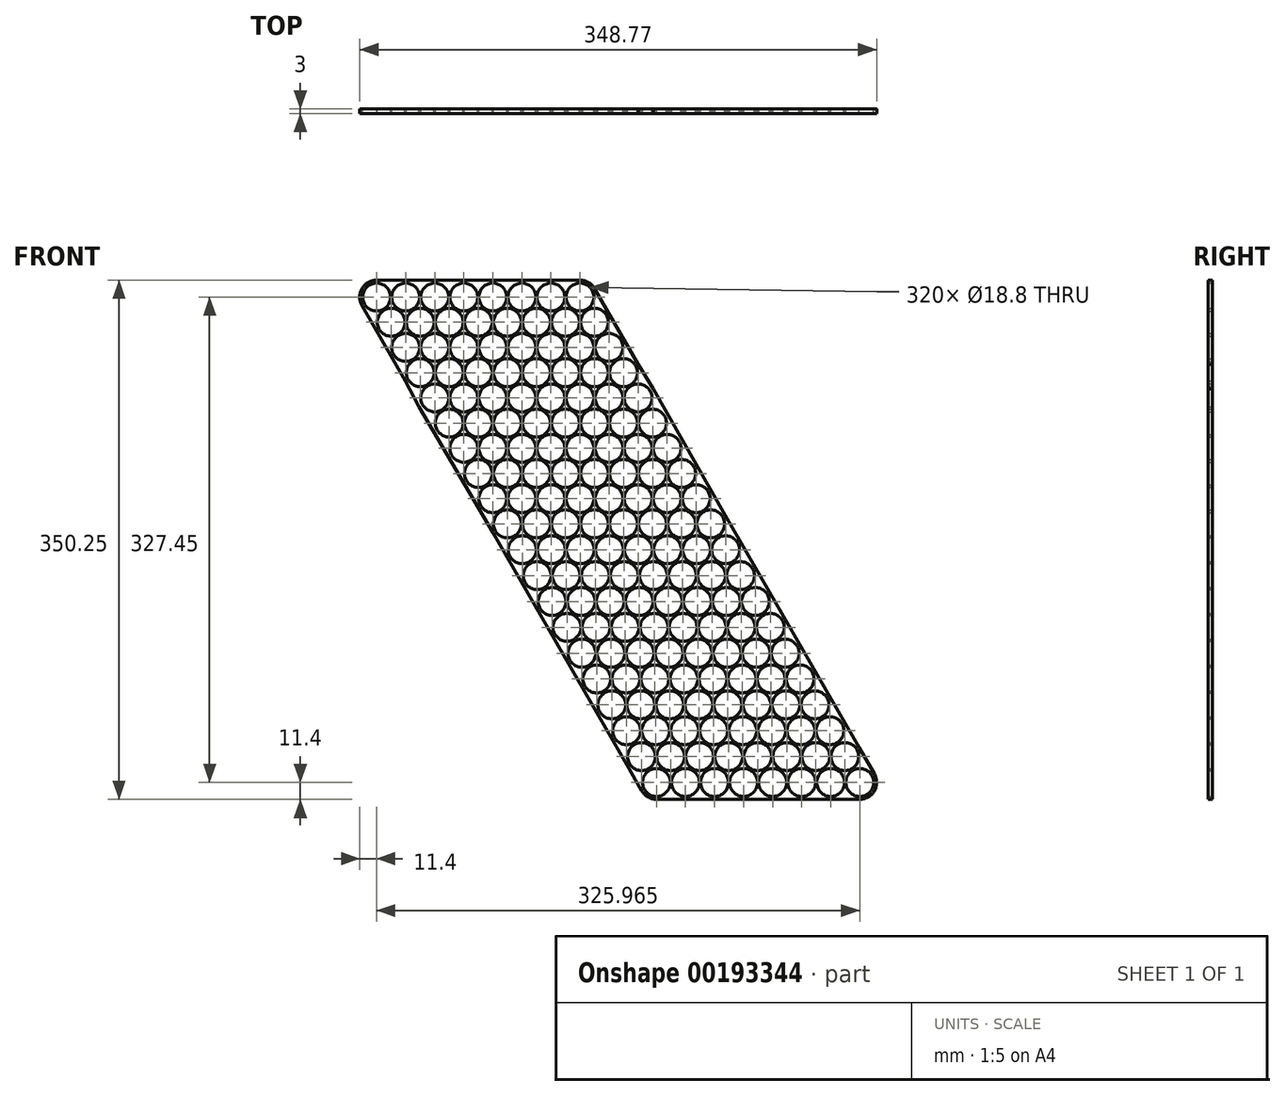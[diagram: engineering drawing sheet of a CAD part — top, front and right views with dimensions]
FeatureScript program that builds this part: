
annotation { "Feature Type Name" : "Feature", "Feature Type Description" : "" }
export const myFeature = defineFeature(function(context is Context, id is Id, definition is map)
    precondition{}
    {
        {
            var Q0;
            Q0=qCreatedBy(makeId("Front.planeOp"),FACE);
            var sketch = newSketch(context, id + "F0", { "sketchPlane" : qUnion([Q0])});
            skCircle(sketch, "E0", {"center": v(0, 0) * mm, "radius": 9.4 * mm});
            skCircle(sketch, "E1.1.0.0", {"center": v(19.6, 0) * mm, "radius": 9.4 * mm});
            skCircle(sketch, "E1.2.0.0", {"center": v(39.2, 0) * mm, "radius": 9.4 * mm});
            skCircle(sketch, "E1.3.0.0", {"center": v(58.8, 0) * mm, "radius": 9.4 * mm});
            skLineSegment(sketch, "E1.direction1", {"start": v(0, 0) * mm, "end": v(19.6, 0) * mm, "construction": true});
            skLineSegment(sketch, "E2", {"start": v(0, -17) * mm, "end": v(73.2, -17) * mm, "construction": true});
            skLineSegment(sketch, "E3", {"start": v(9.8, 0) * mm, "end": v(9.8, -17) * mm, "construction": true});
            skCircle(sketch, "E4", {"center": v(9.8, -17) * mm, "radius": 9.4 * mm});
            skCircle(sketch, "E5.1.0.0", {"center": v(29.4, -17) * mm, "radius": 9.4 * mm});
            skCircle(sketch, "E5.2.0.0", {"center": v(49, -17) * mm, "radius": 9.4 * mm});
            skCircle(sketch, "E5.3.0.0", {"center": v(68.6, -17) * mm, "radius": 9.4 * mm});
            skLineSegment(sketch, "E5.direction1", {"start": v(9.8, -17) * mm, "end": v(29.4, -17) * mm, "construction": true});
            skLineSegment(sketch, "E6", {"start": v(-8.14, -4.7) * mm, "end": v(1.66, -21.7) * mm});
            skLineSegment(sketch, "E7", {"start": v(0, 9.4) * mm, "end": v(58.8, 9.4) * mm});
            skLineSegment(sketch, "E8", {"start": v(9.8, -17) * mm, "end": v(9.8, -26.4) * mm, "construction": true});
            skLineSegment(sketch, "E9", {"start": v(68.6, -17) * mm, "end": v(68.6, -26.4) * mm, "construction": true});
            skArc(sketch, "E10", {"start": v(58.8, 9.4) * mm, "mid": v(63.5, 8.14) * mm, "end": v(66.94, 4.7) * mm});
            skArc(sketch, "E11", {"start": v(76.74, -12.3) * mm, "mid": v(76.74, -21.7) * mm, "end": v(68.6, -26.4) * mm});
            skArc(sketch, "E12", {"start": v(9.8, -26.4) * mm, "mid": v(5.1, -25.14) * mm, "end": v(1.66, -21.7) * mm});
            skArc(sketch, "E13", {"start": v(-8.14, -4.7) * mm, "mid": v(-8.14, 4.7) * mm, "end": v(0, 9.4) * mm});
            skArc(sketch, "E14.0", {"start": v(0, 11.4) * mm, "mid": v(-9.87, 5.7) * mm, "end": v(-9.88, -5.7) * mm});
            skLineSegment(sketch, "E15.0", {"start": v(0, 11.4) * mm, "end": v(58.8, 11.4) * mm});
            skLineSegment(sketch, "E16.0", {"start": v(-9.88, -5.7) * mm, "end": v(-0.08, -22.7) * mm});
            skArc(sketch, "E17.trimOffspring", {"start": v(9.8, -5.82) * mm, "mid": v(9.87, -5.71) * mm, "end": v(9.93, -5.6) * mm});
            skArc(sketch, "E18.trimOffspring", {"start": v(9.93, -5.6) * mm, "mid": v(9.86, -5.6) * mm, "end": v(9.8, -5.6) * mm});
            skCircle(sketch, "E19.0.4.0", {"center": v(78.4, 0) * mm, "radius": 9.4 * mm});
            skCircle(sketch, "E19.0.5.0", {"center": v(98, 0) * mm, "radius": 9.4 * mm});
            skCircle(sketch, "E20.0.4.0", {"center": v(88.2, -17) * mm, "radius": 9.4 * mm});
            skCircle(sketch, "E20.0.5.0", {"center": v(107.8, -17) * mm, "radius": 9.4 * mm});
            skLineSegment(sketch, "E21", {"start": v(58.8, 11.4) * mm, "end": v(98, 11.4) * mm});
            skLineSegment(sketch, "E22", {"start": v(0, 0) * mm, "end": v(9.8, -17) * mm, "construction": true});
            skCircle(sketch, "E23.1.0.0", {"center": v(19.6, -34) * mm, "radius": 9.4 * mm});
            skCircle(sketch, "E23.2.0.0", {"center": v(29.4, -51) * mm, "radius": 9.4 * mm});
            skLineSegment(sketch, "E23.direction1", {"start": v(9.8, -17) * mm, "end": v(19.6, -34) * mm, "construction": true});
            skCircle(sketch, "E24.1.0.0", {"center": v(39.2, -34) * mm, "radius": 9.4 * mm});
            skCircle(sketch, "E24.1.0.1", {"center": v(49, -51) * mm, "radius": 9.4 * mm});
            skCircle(sketch, "E24.2.0.0", {"center": v(58.8, -34) * mm, "radius": 9.4 * mm});
            skCircle(sketch, "E24.2.0.1", {"center": v(68.6, -51) * mm, "radius": 9.4 * mm});
            skCircle(sketch, "E24.3.0.0", {"center": v(78.4, -34) * mm, "radius": 9.4 * mm});
            skCircle(sketch, "E24.3.0.1", {"center": v(88.2, -51) * mm, "radius": 9.4 * mm});
            skCircle(sketch, "E24.4.0.0", {"center": v(98, -34) * mm, "radius": 9.4 * mm});
            skCircle(sketch, "E24.4.0.1", {"center": v(107.8, -51) * mm, "radius": 9.4 * mm});
            skCircle(sketch, "E24.5.0.0", {"center": v(117.6, -34) * mm, "radius": 9.4 * mm});
            skCircle(sketch, "E24.5.0.1", {"center": v(127.4, -51) * mm, "radius": 9.4 * mm});
            skLineSegment(sketch, "E24.direction1", {"start": v(19.6, -34) * mm, "end": v(39.2, -34) * mm, "construction": true});
            skLineSegment(sketch, "E25", {"start": v(-0.08, -22.7) * mm, "end": v(19.52, -56.7) * mm});
            skArc(sketch, "E26.0", {"start": v(29.27, -62.4) * mm, "mid": v(29.33, -62.4) * mm, "end": v(29.4, -62.4) * mm});
            skCircle(sketch, "E27.0.6.0", {"center": v(117.6, 0) * mm, "radius": 9.4 * mm});
            skCircle(sketch, "E27.0.7.0", {"center": v(137.2, 0) * mm, "radius": 9.4 * mm});
            skCircle(sketch, "E28.0.6.0", {"center": v(127.4, -17) * mm, "radius": 9.4 * mm});
            skCircle(sketch, "E28.0.7.0", {"center": v(147, -17) * mm, "radius": 9.4 * mm});
            skCircle(sketch, "E29.0.6.0", {"center": v(137.2, -34) * mm, "radius": 9.4 * mm});
            skCircle(sketch, "E29.2.6.0", {"center": v(147, -51) * mm, "radius": 9.4 * mm});
            skCircle(sketch, "E29.0.7.0", {"center": v(156.8, -34) * mm, "radius": 9.4 * mm});
            skCircle(sketch, "E29.2.7.0", {"center": v(166.6, -51) * mm, "radius": 9.4 * mm});
            skArc(sketch, "E30.0", {"start": v(147.08, 5.7) * mm, "mid": v(142.9, 9.87) * mm, "end": v(137.2, 11.4) * mm});
            skLineSegment(sketch, "E31", {"start": v(98, 11.4) * mm, "end": v(137.2, 11.4) * mm});
            skLineSegment(sketch, "E32", {"start": v(147.08, 5.7) * mm, "end": v(176.48, -45.3) * mm});
            skCircle(sketch, "E33.0.3.0", {"center": v(39.2, -68) * mm, "radius": 9.4 * mm});
            skCircle(sketch, "E34.1.0.0", {"center": v(58.8, -68) * mm, "radius": 9.4 * mm});
            skCircle(sketch, "E34.2.0.0", {"center": v(78.4, -68) * mm, "radius": 9.4 * mm});
            skCircle(sketch, "E34.3.0.0", {"center": v(98, -68) * mm, "radius": 9.4 * mm});
            skCircle(sketch, "E34.4.0.0", {"center": v(117.6, -68) * mm, "radius": 9.4 * mm});
            skCircle(sketch, "E34.5.0.0", {"center": v(137.2, -68) * mm, "radius": 9.4 * mm});
            skCircle(sketch, "E34.6.0.0", {"center": v(156.8, -68) * mm, "radius": 9.4 * mm});
            skCircle(sketch, "E34.7.0.0", {"center": v(176.4, -68) * mm, "radius": 9.4 * mm});
            skLineSegment(sketch, "E34.direction1", {"start": v(39.2, -68) * mm, "end": v(58.8, -68) * mm, "construction": true});
            skLineSegment(sketch, "E35", {"start": v(19.52, -56.7) * mm, "end": v(28.57, -74.14) * mm});
            skLineSegment(sketch, "E36", {"start": v(176.48, -45.3) * mm, "end": v(186.68, -62.07) * mm});
            skCircle(sketch, "E37.1.0.0", {"center": v(49, -85) * mm, "radius": 9.4 * mm});
            skCircle(sketch, "E37.1.0.1", {"center": v(68.6, -85) * mm, "radius": 9.4 * mm});
            skCircle(sketch, "E37.1.0.2", {"center": v(88.2, -85) * mm, "radius": 9.4 * mm});
            skCircle(sketch, "E37.1.0.3", {"center": v(107.8, -85) * mm, "radius": 9.4 * mm});
            skCircle(sketch, "E37.1.0.4", {"center": v(127.4, -85) * mm, "radius": 9.4 * mm});
            skCircle(sketch, "E37.1.0.5", {"center": v(147, -85) * mm, "radius": 9.4 * mm});
            skCircle(sketch, "E37.1.0.6", {"center": v(166.6, -85) * mm, "radius": 9.4 * mm});
            skCircle(sketch, "E37.1.0.7", {"center": v(186.2, -85) * mm, "radius": 9.4 * mm});
            skCircle(sketch, "E37.2.0.0", {"center": v(58.8, -102) * mm, "radius": 9.4 * mm});
            skCircle(sketch, "E37.2.0.1", {"center": v(78.4, -102) * mm, "radius": 9.4 * mm});
            skCircle(sketch, "E37.2.0.2", {"center": v(98, -102) * mm, "radius": 9.4 * mm});
            skCircle(sketch, "E37.2.0.3", {"center": v(117.6, -102) * mm, "radius": 9.4 * mm});
            skCircle(sketch, "E37.2.0.4", {"center": v(137.2, -102) * mm, "radius": 9.4 * mm});
            skCircle(sketch, "E37.2.0.5", {"center": v(156.8, -102) * mm, "radius": 9.4 * mm});
            skCircle(sketch, "E37.2.0.6", {"center": v(176.4, -102) * mm, "radius": 9.4 * mm});
            skCircle(sketch, "E37.2.0.7", {"center": v(196, -102) * mm, "radius": 9.4 * mm});
            skCircle(sketch, "E37.3.0.0", {"center": v(68.6, -119) * mm, "radius": 9.4 * mm});
            skCircle(sketch, "E37.3.0.1", {"center": v(88.2, -119) * mm, "radius": 9.4 * mm});
            skCircle(sketch, "E37.3.0.2", {"center": v(107.8, -119) * mm, "radius": 9.4 * mm});
            skCircle(sketch, "E37.3.0.3", {"center": v(127.4, -119) * mm, "radius": 9.4 * mm});
            skCircle(sketch, "E37.3.0.4", {"center": v(147, -119) * mm, "radius": 9.4 * mm});
            skCircle(sketch, "E37.3.0.5", {"center": v(166.6, -119) * mm, "radius": 9.4 * mm});
            skCircle(sketch, "E37.3.0.6", {"center": v(186.2, -119) * mm, "radius": 9.4 * mm});
            skCircle(sketch, "E37.3.0.7", {"center": v(205.8, -119) * mm, "radius": 9.4 * mm});
            skCircle(sketch, "E37.4.0.0", {"center": v(78.4, -136) * mm, "radius": 9.4 * mm});
            skCircle(sketch, "E37.4.0.1", {"center": v(98, -136) * mm, "radius": 9.4 * mm});
            skCircle(sketch, "E37.4.0.2", {"center": v(117.6, -136) * mm, "radius": 9.4 * mm});
            skCircle(sketch, "E37.4.0.3", {"center": v(137.2, -136) * mm, "radius": 9.4 * mm});
            skCircle(sketch, "E37.4.0.4", {"center": v(156.8, -136) * mm, "radius": 9.4 * mm});
            skCircle(sketch, "E37.4.0.5", {"center": v(176.4, -136) * mm, "radius": 9.4 * mm});
            skCircle(sketch, "E37.4.0.6", {"center": v(196, -136) * mm, "radius": 9.4 * mm});
            skCircle(sketch, "E37.4.0.7", {"center": v(215.6, -136) * mm, "radius": 9.4 * mm});
            skCircle(sketch, "E37.5.0.0", {"center": v(88.2, -153) * mm, "radius": 9.4 * mm});
            skCircle(sketch, "E37.5.0.1", {"center": v(107.8, -153) * mm, "radius": 9.4 * mm});
            skCircle(sketch, "E37.5.0.2", {"center": v(127.4, -153) * mm, "radius": 9.4 * mm});
            skCircle(sketch, "E37.5.0.3", {"center": v(147, -153) * mm, "radius": 9.4 * mm});
            skCircle(sketch, "E37.5.0.4", {"center": v(166.6, -153) * mm, "radius": 9.4 * mm});
            skCircle(sketch, "E37.5.0.5", {"center": v(186.2, -153) * mm, "radius": 9.4 * mm});
            skCircle(sketch, "E37.5.0.6", {"center": v(205.8, -153) * mm, "radius": 9.4 * mm});
            skCircle(sketch, "E37.5.0.7", {"center": v(225.4, -153) * mm, "radius": 9.4 * mm});
            skLineSegment(sketch, "E37.direction1", {"start": v(39.2, -68) * mm, "end": v(49, -85) * mm, "construction": true});
            skLineSegment(sketch, "E38", {"start": v(28.57, -74.14) * mm, "end": v(78.37, -158.78) * mm});
            skLineSegment(sketch, "E39", {"start": v(186.68, -62.07) * mm, "end": v(235.3, -147.35) * mm});
            skCircle(sketch, "E40.1.0.0", {"center": v(98.25, -170.44) * mm, "radius": 9.4 * mm});
            skCircle(sketch, "E40.1.0.1", {"center": v(117.85, -170.44) * mm, "radius": 9.4 * mm});
            skCircle(sketch, "E40.1.0.2", {"center": v(137.45, -170.44) * mm, "radius": 9.4 * mm});
            skCircle(sketch, "E40.1.0.3", {"center": v(157.05, -170.44) * mm, "radius": 9.4 * mm});
            skCircle(sketch, "E40.1.0.4", {"center": v(176.65, -170.44) * mm, "radius": 9.4 * mm});
            skCircle(sketch, "E40.1.0.5", {"center": v(196.25, -170.44) * mm, "radius": 9.4 * mm});
            skCircle(sketch, "E40.1.0.6", {"center": v(215.85, -170.44) * mm, "radius": 9.4 * mm});
            skCircle(sketch, "E40.1.0.7", {"center": v(235.45, -170.44) * mm, "radius": 9.4 * mm});
            skCircle(sketch, "E40.2.0.0", {"center": v(108.31, -187.89) * mm, "radius": 9.4 * mm});
            skCircle(sketch, "E40.2.0.1", {"center": v(127.91, -187.89) * mm, "radius": 9.4 * mm});
            skCircle(sketch, "E40.2.0.2", {"center": v(147.51, -187.89) * mm, "radius": 9.4 * mm});
            skCircle(sketch, "E40.2.0.3", {"center": v(167.11, -187.89) * mm, "radius": 9.4 * mm});
            skCircle(sketch, "E40.2.0.4", {"center": v(186.71, -187.89) * mm, "radius": 9.4 * mm});
            skCircle(sketch, "E40.2.0.5", {"center": v(206.31, -187.89) * mm, "radius": 9.4 * mm});
            skCircle(sketch, "E40.2.0.6", {"center": v(225.91, -187.89) * mm, "radius": 9.4 * mm});
            skCircle(sketch, "E40.2.0.7", {"center": v(245.51, -187.89) * mm, "radius": 9.4 * mm});
            skCircle(sketch, "E40.3.0.0", {"center": v(118.37, -205.33) * mm, "radius": 9.4 * mm});
            skCircle(sketch, "E40.3.0.1", {"center": v(137.97, -205.33) * mm, "radius": 9.4 * mm});
            skCircle(sketch, "E40.3.0.2", {"center": v(157.57, -205.33) * mm, "radius": 9.4 * mm});
            skCircle(sketch, "E40.3.0.3", {"center": v(177.17, -205.33) * mm, "radius": 9.4 * mm});
            skCircle(sketch, "E40.3.0.4", {"center": v(196.77, -205.33) * mm, "radius": 9.4 * mm});
            skCircle(sketch, "E40.3.0.5", {"center": v(216.37, -205.33) * mm, "radius": 9.4 * mm});
            skCircle(sketch, "E40.3.0.6", {"center": v(235.97, -205.33) * mm, "radius": 9.4 * mm});
            skCircle(sketch, "E40.3.0.7", {"center": v(255.57, -205.33) * mm, "radius": 9.4 * mm});
            skCircle(sketch, "E40.4.0.0", {"center": v(128.43, -222.78) * mm, "radius": 9.4 * mm});
            skCircle(sketch, "E40.4.0.1", {"center": v(148.03, -222.78) * mm, "radius": 9.4 * mm});
            skCircle(sketch, "E40.4.0.2", {"center": v(167.63, -222.78) * mm, "radius": 9.4 * mm});
            skCircle(sketch, "E40.4.0.3", {"center": v(187.23, -222.78) * mm, "radius": 9.4 * mm});
            skCircle(sketch, "E40.4.0.4", {"center": v(206.83, -222.78) * mm, "radius": 9.4 * mm});
            skCircle(sketch, "E40.4.0.5", {"center": v(226.43, -222.78) * mm, "radius": 9.4 * mm});
            skCircle(sketch, "E40.4.0.6", {"center": v(246.03, -222.78) * mm, "radius": 9.4 * mm});
            skCircle(sketch, "E40.4.0.7", {"center": v(265.63, -222.78) * mm, "radius": 9.4 * mm});
            skCircle(sketch, "E40.5.0.0", {"center": v(138.48, -240.22) * mm, "radius": 9.4 * mm});
            skCircle(sketch, "E40.5.0.1", {"center": v(158.08, -240.22) * mm, "radius": 9.4 * mm});
            skCircle(sketch, "E40.5.0.2", {"center": v(177.68, -240.22) * mm, "radius": 9.4 * mm});
            skCircle(sketch, "E40.5.0.3", {"center": v(197.28, -240.22) * mm, "radius": 9.4 * mm});
            skCircle(sketch, "E40.5.0.4", {"center": v(216.88, -240.22) * mm, "radius": 9.4 * mm});
            skCircle(sketch, "E40.5.0.5", {"center": v(236.48, -240.22) * mm, "radius": 9.4 * mm});
            skCircle(sketch, "E40.5.0.6", {"center": v(256.08, -240.22) * mm, "radius": 9.4 * mm});
            skCircle(sketch, "E40.5.0.7", {"center": v(275.68, -240.22) * mm, "radius": 9.4 * mm});
            skCircle(sketch, "E40.6.0.0", {"center": v(148.54, -257.67) * mm, "radius": 9.4 * mm});
            skCircle(sketch, "E40.6.0.1", {"center": v(168.14, -257.67) * mm, "radius": 9.4 * mm});
            skCircle(sketch, "E40.6.0.2", {"center": v(187.74, -257.67) * mm, "radius": 9.4 * mm});
            skCircle(sketch, "E40.6.0.3", {"center": v(207.34, -257.67) * mm, "radius": 9.4 * mm});
            skCircle(sketch, "E40.6.0.4", {"center": v(226.94, -257.67) * mm, "radius": 9.4 * mm});
            skCircle(sketch, "E40.6.0.5", {"center": v(246.54, -257.67) * mm, "radius": 9.4 * mm});
            skCircle(sketch, "E40.6.0.6", {"center": v(266.14, -257.67) * mm, "radius": 9.4 * mm});
            skCircle(sketch, "E40.6.0.7", {"center": v(285.74, -257.67) * mm, "radius": 9.4 * mm});
            skCircle(sketch, "E40.7.0.0", {"center": v(158.6, -275.11) * mm, "radius": 9.4 * mm});
            skCircle(sketch, "E40.7.0.1", {"center": v(178.2, -275.11) * mm, "radius": 9.4 * mm});
            skCircle(sketch, "E40.7.0.2", {"center": v(197.8, -275.11) * mm, "radius": 9.4 * mm});
            skCircle(sketch, "E40.7.0.3", {"center": v(217.4, -275.11) * mm, "radius": 9.4 * mm});
            skCircle(sketch, "E40.7.0.4", {"center": v(237, -275.11) * mm, "radius": 9.4 * mm});
            skCircle(sketch, "E40.7.0.5", {"center": v(256.6, -275.11) * mm, "radius": 9.4 * mm});
            skCircle(sketch, "E40.7.0.6", {"center": v(276.2, -275.11) * mm, "radius": 9.4 * mm});
            skCircle(sketch, "E40.7.0.7", {"center": v(295.8, -275.11) * mm, "radius": 9.4 * mm});
            skCircle(sketch, "E40.8.0.0", {"center": v(168.65, -292.56) * mm, "radius": 9.4 * mm});
            skCircle(sketch, "E40.8.0.1", {"center": v(188.25, -292.56) * mm, "radius": 9.4 * mm});
            skCircle(sketch, "E40.8.0.2", {"center": v(207.85, -292.56) * mm, "radius": 9.4 * mm});
            skCircle(sketch, "E40.8.0.3", {"center": v(227.45, -292.56) * mm, "radius": 9.4 * mm});
            skCircle(sketch, "E40.8.0.4", {"center": v(247.05, -292.56) * mm, "radius": 9.4 * mm});
            skCircle(sketch, "E40.8.0.5", {"center": v(266.65, -292.56) * mm, "radius": 9.4 * mm});
            skCircle(sketch, "E40.8.0.6", {"center": v(286.25, -292.56) * mm, "radius": 9.4 * mm});
            skCircle(sketch, "E40.8.0.7", {"center": v(305.85, -292.56) * mm, "radius": 9.4 * mm});
            skCircle(sketch, "E40.9.0.0", {"center": v(178.7, -310) * mm, "radius": 9.4 * mm});
            skCircle(sketch, "E40.9.0.1", {"center": v(198.3, -310) * mm, "radius": 9.4 * mm});
            skCircle(sketch, "E40.9.0.2", {"center": v(217.9, -310) * mm, "radius": 9.4 * mm});
            skCircle(sketch, "E40.9.0.3", {"center": v(237.5, -310) * mm, "radius": 9.4 * mm});
            skCircle(sketch, "E40.9.0.4", {"center": v(257.1, -310) * mm, "radius": 9.4 * mm});
            skCircle(sketch, "E40.9.0.5", {"center": v(276.7, -310) * mm, "radius": 9.4 * mm});
            skCircle(sketch, "E40.9.0.6", {"center": v(296.3, -310) * mm, "radius": 9.4 * mm});
            skCircle(sketch, "E40.9.0.7", {"center": v(315.9, -310) * mm, "radius": 9.4 * mm});
            skLineSegment(sketch, "E40.direction1", {"start": v(88.2, -153) * mm, "end": v(98.25, -170.44) * mm, "construction": true});
            skLineSegment(sketch, "E41.0", {"start": v(168.83, -315.7) * mm, "end": v(168.83, -315.7) * mm});
            skLineSegment(sketch, "E42", {"start": v(235.3, -147.35) * mm, "end": v(325.79, -304.31) * mm});
            skLineSegment(sketch, "E43", {"start": v(78.37, -158.78) * mm, "end": v(168.83, -315.7) * mm});
            skCircle(sketch, "E44.0.10.0", {"center": v(188.77, -327.45) * mm, "radius": 9.4 * mm});
            skCircle(sketch, "E44.2.10.0", {"center": v(208.37, -327.45) * mm, "radius": 9.4 * mm});
            skCircle(sketch, "E44.4.10.0", {"center": v(227.97, -327.45) * mm, "radius": 9.4 * mm});
            skCircle(sketch, "E44.6.10.0", {"center": v(247.57, -327.45) * mm, "radius": 9.4 * mm});
            skCircle(sketch, "E44.8.10.0", {"center": v(267.17, -327.45) * mm, "radius": 9.4 * mm});
            skCircle(sketch, "E44.10.10.0", {"center": v(286.77, -327.45) * mm, "radius": 9.4 * mm});
            skCircle(sketch, "E44.12.10.0", {"center": v(306.37, -327.45) * mm, "radius": 9.4 * mm});
            skCircle(sketch, "E44.14.10.0", {"center": v(325.97, -327.45) * mm, "radius": 9.4 * mm});
            skArc(sketch, "E45.0", {"start": v(178.89, -333.14) * mm, "mid": v(183.06, -337.32) * mm, "end": v(188.77, -338.85) * mm});
            skArc(sketch, "E46.0", {"start": v(325.97, -338.85) * mm, "mid": v(335.84, -333.15) * mm, "end": v(335.84, -321.76) * mm});
            skLineSegment(sketch, "E47", {"start": v(168.83, -315.7) * mm, "end": v(178.89, -333.14) * mm});
            skLineSegment(sketch, "E48", {"start": v(325.79, -304.31) * mm, "end": v(335.84, -321.76) * mm});
            skLineSegment(sketch, "E49", {"start": v(188.77, -338.85) * mm, "end": v(325.97, -338.85) * mm});
            skLineSegment(sketch, "E50.trimOffspring", {"start": v(325.79, -304.31) * mm, "end": v(325.79, -304.31) * mm});
            skSolve(sketch);
        }
        {
            var Q0;
            Q0=makeQuery(id+"F0.imprint","IMPRINT",FACE,{"disambiguationData":[TD([[makeQuery(id+"F0.imprint","IMPRINT",EDGE,{"derivedFrom":sQuery(id+"F0.wireOp",EDGE,"E1.1.0.0")}),-1.0]])]});
            extrude(context, id + "F1", {"entities" : qUnion([Q0]), "depth" : 3 * mm});
        }
    });
